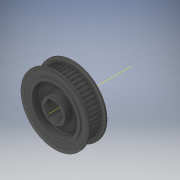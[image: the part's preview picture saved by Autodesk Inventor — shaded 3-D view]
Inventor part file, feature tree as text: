
AUTODESK INVENTOR PART (.ipt)
format: ipt  version: 2019.4 (Build 234330000, 330)  size: 578,048 bytes
history: native  units: in
note: dims shown in document units (in); Inventor stores cm internally (conversion verified against a paired STEP export)
features: other x1, fillet x1
ambient origin geometry x8: Origin, YZ Plane, XZ Plane, XY Plane, X Axis, Y Axis, Z Axis, Center Point
bodies: Solid1 (feature_tree)
feature tree (2):
  other  "Work Axis1"
  fillet  "Fillet1"  [1 undecoded]
note: 1 required parameter value undecoded (feature->parameter linkage not recoverable at this tier; creation-order binding heuristic only, values carry confidence <= 0.55)
